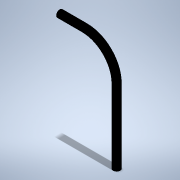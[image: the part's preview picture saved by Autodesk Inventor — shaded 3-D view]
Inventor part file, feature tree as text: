
AUTODESK INVENTOR PART (.ipt)
format: ipt  version: 2022.2 (Build 262287010, 287A)  size: 112,128 bytes
history: native  units: mm
features: reference x5, other x4, sketch x2, sweep x1
ambient origin geometry x8: Origin, YZ Plane, XZ Plane, XY Plane, X Axis, Y Axis, Z Axis, Center Point
bodies: Solid1 (feature_tree)
feature tree (12):
  sweep  "Sweep1"
  sketch  "Sketch1"  dims[d0=18.0mm d1=0.0mm d2=0.0mm]
  reference  "Reference1"
  reference  "Reference2"
  reference  "Reference3"
  reference  "Reference4"
  sketch  "Sketch2"
  reference  "Reference5"
  parser-record x1  (decoder bookkeeping rows leaked as tree rows — omitted from the tree; the rows remain in map.json)
  other  "ND.BaseBoard._Main.iam"
  other  "1216.1001_head:1"
  other  "Crystal:1"
note: 1 file-system path scrubbed to <path> (originals preserved in map.json)
